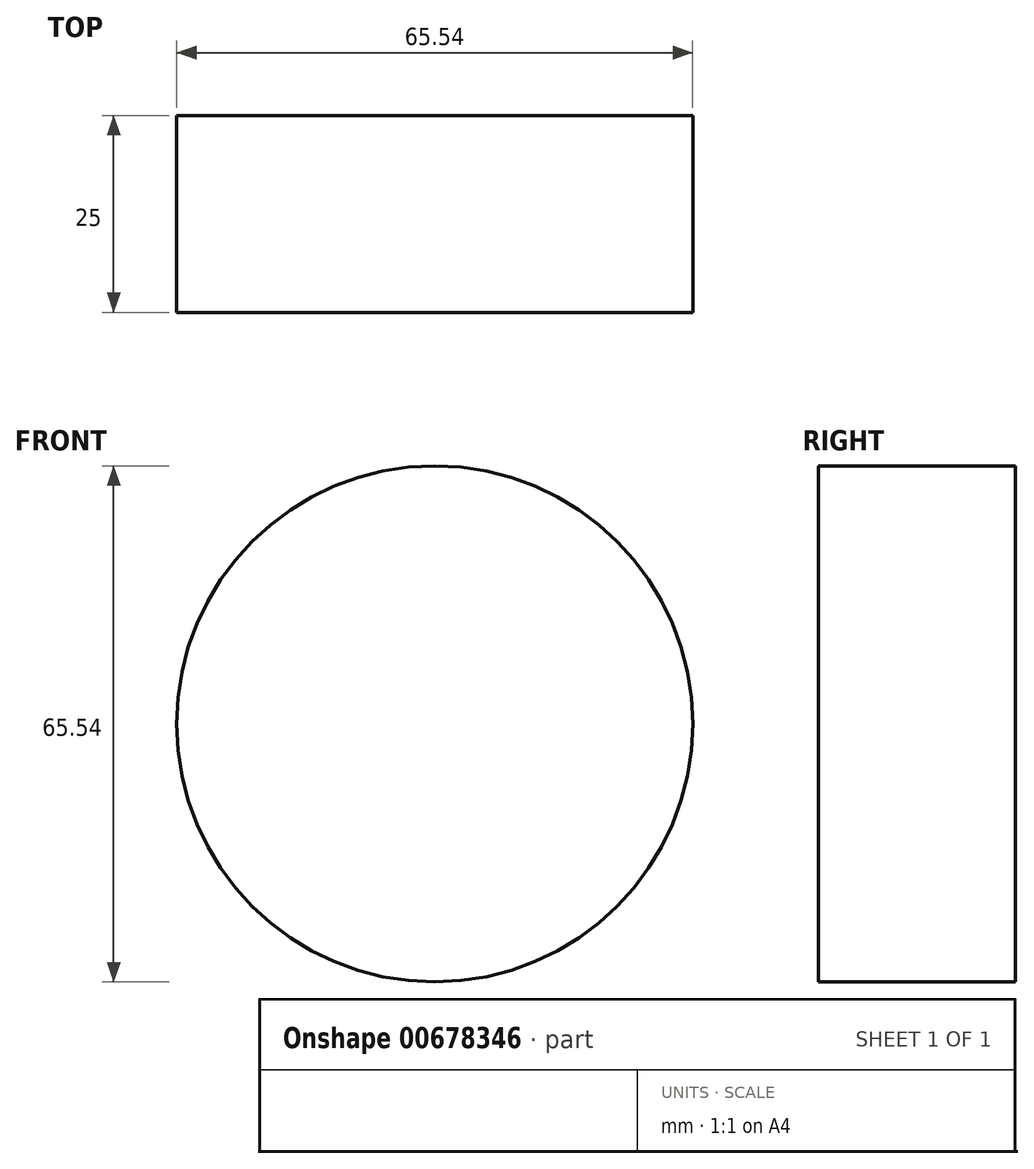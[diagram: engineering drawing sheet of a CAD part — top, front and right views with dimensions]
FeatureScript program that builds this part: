
annotation { "Feature Type Name" : "Feature", "Feature Type Description" : "" }
export const myFeature = defineFeature(function(context is Context, id is Id, definition is map)
    precondition{}
    {
        {
            var Q0;
            Q0=qCreatedBy(makeId("Front.planeOp"),FACE);
            var sketch = newSketch(context, id + "F0", { "sketchPlane" : qUnion([Q0])});
            skCircle(sketch, "E0", {"center": v(0, -2.3) * mm, "radius": 32.77 * mm});
            skSolve(sketch);
        }
        {
            var Q0;
            Q0 = qSketchRegion(id + "F0", true);
            extrude(context, id + "F1", {"entities" : qUnion([Q0]), "depth" : 25 * mm, "offsetDistance" : 25 * mm});
        }
        {
            var Q0;
            Q0=qCreatedBy(makeId("Front.planeOp"),FACE);
            var sketch = newSketch(context, id + "F2", { "sketchPlane" : qUnion([Q0])});
            skCircle(sketch, "E1", {"center": v(0, -2.56) * mm, "radius": 2.98 * mm});
            skSolve(sketch);
        }
        {
            var Q0;
            Q0=sQuery(id+"F2.wireOp",EDGE,"E1");
            extrude(context, id + "F3", {"bodyType" : ToolBodyType.SURFACE, "surfaceEntities" : qUnion([Q0]), "depth" : 25 * mm, "offsetDistance" : 25 * mm});
        }
        {
            var Q0;
            Q0=qCreatedBy(makeId("Front.planeOp"),FACE);
            var sketch = newSketch(context, id + "F4", { "sketchPlane" : qUnion([Q0])});
            skCircle(sketch, "E2", {"center": v(0, -2.36) * mm, "radius": 2.52 * mm});
            skSolve(sketch);
        }
        {
            var Q0;
            Q0 = qSketchRegion(id + "F4", true);
            extrude(context, id + "F5", {"entities" : qUnion([Q0]), "operationType" : NewBodyOperationType.ADD, "depth" : 25 * mm, "offsetDistance" : 25 * mm});
        }
    });
